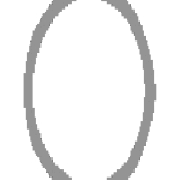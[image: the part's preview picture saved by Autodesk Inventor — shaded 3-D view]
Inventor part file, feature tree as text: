
AUTODESK INVENTOR PART (.ipt)
format: ipt  version: 2021 (Build 250183000, 183)  size: 109,056 bytes
history: native  units: in
note: dims shown in document units (in); Inventor stores cm internally (conversion verified against a paired STEP export)
features: other x4, sketch x3, plane x1
ambient origin geometry x8: Origin, YZ Plane, XZ Plane, XY Plane, X Axis, Y Axis, Z Axis, Center Point
bodies: Solid1 (feature_tree), Body (feature_tree)
feature tree (8):
  other  "Driven Length"
  other  "Frame Generator"
  other  "Start Plane"
  other  "End Plane"
  sketch  "Sketch"  dims[d2=20.0811in d4=-0.0in d5=20.0811in d6=0.12in d7=0.0in d8=90.0deg d9=20.0811in]
  sketch  "Sketch2"  dims[d0=1.0in]
  plane  "Work Plane3"
  sketch  "Sketch3"  dims[d1=0.065in]
